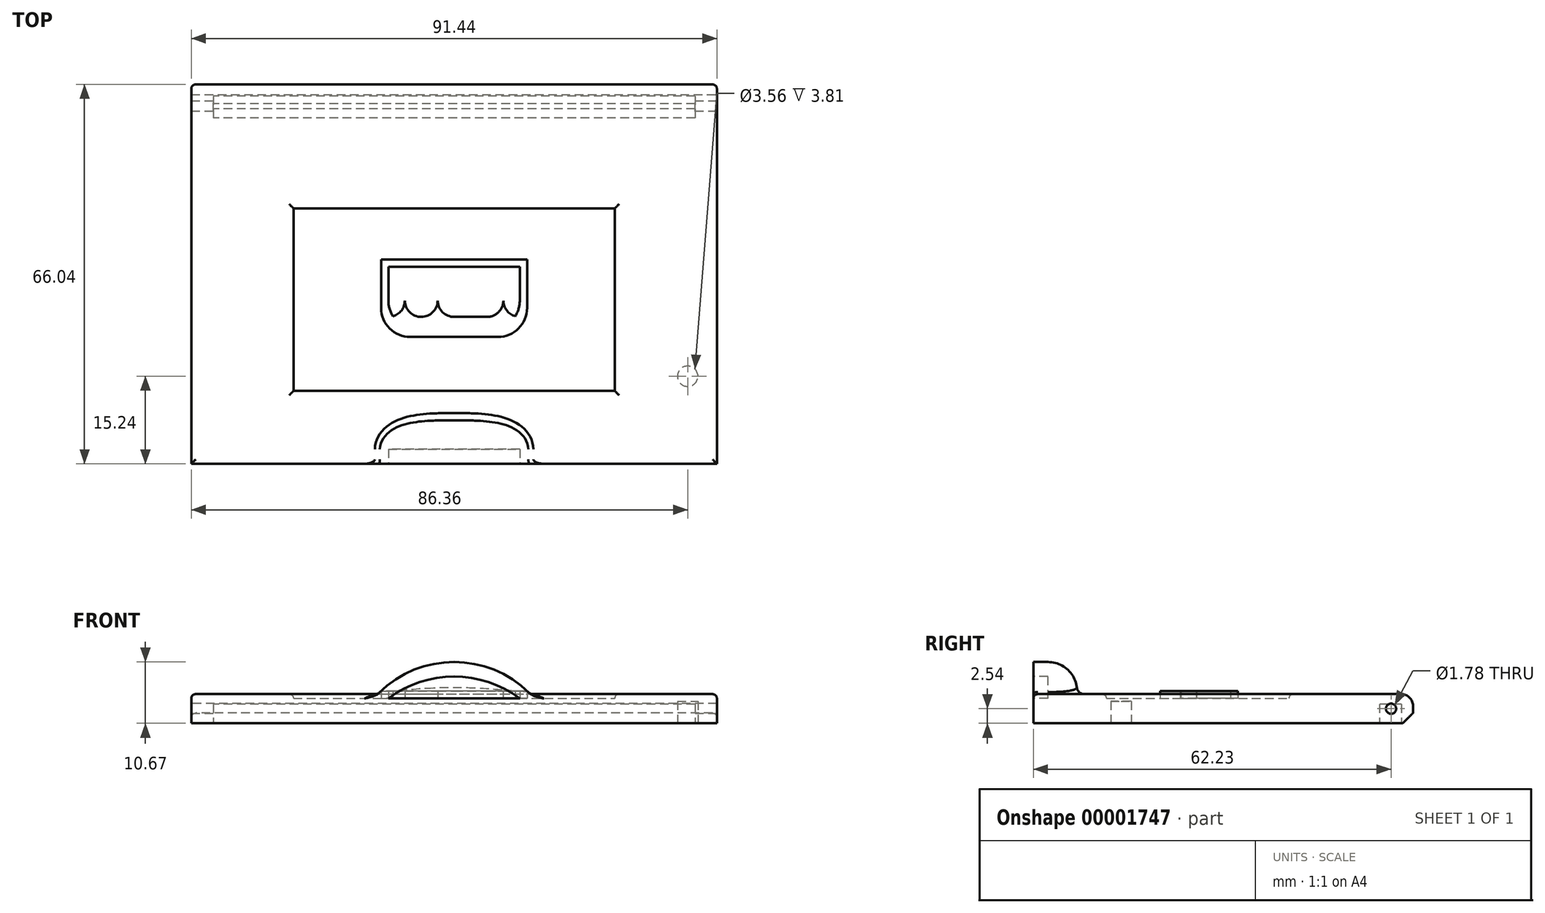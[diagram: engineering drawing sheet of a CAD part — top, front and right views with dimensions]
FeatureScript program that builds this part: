
annotation { "Feature Type Name" : "Feature", "Feature Type Description" : "" }
export const myFeature = defineFeature(function(context is Context, id is Id, definition is map)
    precondition{}
    {
        {
            var Q0;
            Q0=qCreatedBy(makeId("Top.planeOp"),FACE);
            var sketch = newSketch(context, id + "F0", { "sketchPlane" : qUnion([Q0])});
            skLineSegment(sketch, "E0.bottom", {"start": v(0, 0) * mm, "end": v(91.44, 0) * mm});
            skLineSegment(sketch, "E0.top", {"start": v(0, 66.04) * mm, "end": v(91.44, 66.04) * mm});
            skLineSegment(sketch, "E0.left", {"start": v(0, 0) * mm, "end": v(0, 66.04) * mm});
            skLineSegment(sketch, "E0.right", {"start": v(91.44, 0) * mm, "end": v(91.44, 66.04) * mm});
            skSolve(sketch);
        }
        {
            var Q0;
            Q0 = qSketchRegion(id + "F0", true);
            extrude(context, id + "F1", {"entities" : qUnion([Q0]), "depth" : 5.08 * mm});
        }
        {
            var Q0;
            Q0=makeQuery(id+"F1.opExtrude","SWEPT_FACE",FACE,{"disambiguationData":[OSD([sQuery(id+"F0.wireOp",EDGE,"E0.left")])]});
            var sketch = newSketch(context, id + "F2", { "sketchPlane" : qUnion([Q0])});
            skLineSegment(sketch, "E1", {"start": v(-66.04, 2.54) * mm, "end": v(-62.23, 2.54) * mm, "construction": true});
            skCircle(sketch, "E2", {"center": v(-62.23, 2.54) * mm, "radius": 0.89 * mm});
            skSolve(sketch);
        }
        {
            var Q0;
            Q0 = qSketchRegion(id + "F2", true);
            extrude(context, id + "F3", {"entities" : qUnion([Q0]), "operationType" : NewBodyOperationType.REMOVE, "oppositeDirection" : true, "depth" : 91.44 * mm});
        }
        {
            var Q0;
            Q0=makeQuery(id+"F1.opExtrude","CAP_FACE",FACE,{"disambiguationData":[OSD([sQuery(id+"F0.wireOp",EDGE,"E0.bottom"),sQuery(id+"F0.wireOp",EDGE,"E0.top"),sQuery(id+"F0.wireOp",EDGE,"E0.left"),sQuery(id+"F0.wireOp",EDGE,"E0.right")])],"isStart":true});
            var sketch = newSketch(context, id + "F4", { "sketchPlane" : qUnion([Q0])});
            skLineSegment(sketch, "E3", {"start": v(91.44, -66.04) * mm, "end": v(87.63, -66.04) * mm, "construction": true});
            skLineSegment(sketch, "E4", {"start": v(87.63, -66.04) * mm, "end": v(87.63, -64) * mm, "construction": true});
            skSolve(sketch);
        }
        {
            var Q0;
            Q0=makeQuery(id+"F4.imprint","IMPRINT",FACE,{"disambiguationData":[TD([[makeQuery(id+"F4.imprint","IMPRINT",EDGE,{"derivedFrom":makeQuery(id+"F1.opExtrude","CAP_EDGE",EDGE,{"disambiguationData":[OSD([sQuery(id+"F0.wireOp",EDGE,"E0.bottom")])],"isStart":true})}),-1.0]])]});
            var sketch = newSketch(context, id + "F5", { "sketchPlane" : qUnion([Q0])});
            skLineSegment(sketch, "E5.bottom", {"start": v(87.63, -64) * mm, "end": v(3.81, -64) * mm});
            skLineSegment(sketch, "E5.top", {"start": v(87.63, -60.2) * mm, "end": v(3.81, -60.2) * mm});
            skLineSegment(sketch, "E5.left", {"start": v(87.63, -64) * mm, "end": v(87.63, -60.2) * mm});
            skLineSegment(sketch, "E5.right", {"start": v(3.81, -64) * mm, "end": v(3.81, -60.2) * mm});
            skSolve(sketch);
        }
        {
            var Q0;
            Q0 = qSketchRegion(id + "F5", true);
            extrude(context, id + "F6", {"entities" : qUnion([Q0]), "operationType" : NewBodyOperationType.REMOVE, "oppositeDirection" : true, "depth" : 3.3 * mm});
        }
        {
            var Q0;
            Q0=makeQuery(id+"F1.opExtrude","CAP_EDGE",EDGE,{"disambiguationData":[OSD([sQuery(id+"F0.wireOp",EDGE,"E0.top")])],"isStart":true});
            chamfer(context, id + "F7", {"entities" : qUnion([Q0]), "width" : 1.78 * mm, "tangentPropagation" : true});
        }
        {
            var Q0;
            Q0=makeQuery(id+"F1.opExtrude","CAP_EDGE",EDGE,{"disambiguationData":[OSD([sQuery(id+"F0.wireOp",EDGE,"E0.top")])],"isStart":false});
            fillet(context, id + "F8", {"entities" : qUnion([Q0]), "radius" : 2.03 * mm, "tangentPropagation" : true, "allowEdgeOverflow" : false});
        }
        {
            var Q0;
            Q0=makeQuery(id+"F4.imprint","IMPRINT",FACE,{"disambiguationData":[TD([[makeQuery(id+"F4.imprint","IMPRINT",EDGE,{"derivedFrom":makeQuery(id+"F1.opExtrude","CAP_EDGE",EDGE,{"disambiguationData":[OSD([sQuery(id+"F0.wireOp",EDGE,"E0.bottom")])],"isStart":true})}),-1.0]])]});
            var sketch = newSketch(context, id + "F9", { "sketchPlane" : qUnion([Q0])});
            skLineSegment(sketch, "E6", {"start": v(91.44, 0) * mm, "end": v(91.44, -15.24) * mm, "construction": true});
            skLineSegment(sketch, "E7", {"start": v(91.44, -15.24) * mm, "end": v(86.36, -15.24) * mm, "construction": true});
            skSolve(sketch);
        }
        {
            var Q0;
            Q0=makeQuery(id+"F4.imprint","IMPRINT",FACE,{"disambiguationData":[TD([[makeQuery(id+"F4.imprint","IMPRINT",EDGE,{"derivedFrom":makeQuery(id+"F1.opExtrude","CAP_EDGE",EDGE,{"disambiguationData":[OSD([sQuery(id+"F0.wireOp",EDGE,"E0.bottom")])],"isStart":true})}),-1.0]])]});
            var sketch = newSketch(context, id + "F10", { "sketchPlane" : qUnion([Q0])});
            skCircle(sketch, "E8", {"center": v(86.36, -15.24) * mm, "radius": 1.78 * mm});
            skSolve(sketch);
        }
        {
            var Q0;
            Q0 = qSketchRegion(id + "F10", true);
            extrude(context, id + "F11", {"entities" : qUnion([Q0]), "operationType" : NewBodyOperationType.REMOVE, "oppositeDirection" : true, "depth" : 3.8 * mm});
        }
        {
            var Q0;
            Q0=makeQuery(id+"F1.opExtrude","CAP_FACE",FACE,{"disambiguationData":[OSD([sQuery(id+"F0.wireOp",EDGE,"E0.bottom"),sQuery(id+"F0.wireOp",EDGE,"E0.top"),sQuery(id+"F0.wireOp",EDGE,"E0.left"),sQuery(id+"F0.wireOp",EDGE,"E0.right")])],"isStart":false});
            var sketch = newSketch(context, id + "F12", { "sketchPlane" : qUnion([Q0])});
            skLineSegment(sketch, "E9", {"start": v(0, 0) * mm, "end": v(0, 12.7) * mm, "construction": true});
            skLineSegment(sketch, "E10", {"start": v(0, 12.7) * mm, "end": v(17.78, 12.7) * mm});
            skSolve(sketch);
        }
        {
            var Q0;
            {var subQ4=sQuery(id+"F0.wireOp",EDGE,"E0.bottom");var subQ7=makeQuery(id+"F1.opExtrude","CAP_EDGE",EDGE,{"disambiguationData":[OSD([subQ4])],"isStart":false});Q0=makeQuery(id+"F12.imprint","IMPRINT",FACE,{"disambiguationData":[TD([[makeQuery(id+"F12.imprint","IMPRINT",EDGE,{"derivedFrom":subQ7}),1.0]])]});}
            var sketch = newSketch(context, id + "F13", { "sketchPlane" : qUnion([Q0])});
            skLineSegment(sketch, "E11.bottom", {"start": v(17.78, 12.7) * mm, "end": v(73.66, 12.7) * mm});
            skLineSegment(sketch, "E11.top", {"start": v(17.78, 44.45) * mm, "end": v(73.66, 44.45) * mm});
            skLineSegment(sketch, "E11.left", {"start": v(17.78, 12.7) * mm, "end": v(17.78, 44.45) * mm});
            skLineSegment(sketch, "E11.right", {"start": v(73.66, 12.7) * mm, "end": v(73.66, 44.45) * mm});
            skSolve(sketch);
        }
        {
            var Q0;
            Q0 = qSketchRegion(id + "F13", true);
            extrude(context, id + "F14", {"entities" : qUnion([Q0]), "operationType" : NewBodyOperationType.REMOVE, "oppositeDirection" : true, "depth" : 0.76 * mm});
        }
        {
            var Q0;
            Q0=makeQuery(id+"F1.opExtrude","CAP_FACE",FACE,{"disambiguationData":[OSD([sQuery(id+"F0.wireOp",EDGE,"E0.bottom"),sQuery(id+"F0.wireOp",EDGE,"E0.top"),sQuery(id+"F0.wireOp",EDGE,"E0.left"),sQuery(id+"F0.wireOp",EDGE,"E0.right")])],"isStart":false});
            fillet(context, id + "F15", {"entities" : qUnion([Q0]), "radius" : 0.76 * mm, "tangentPropagation" : true, "allowEdgeOverflow" : false});
        }
        {
            var Q0;
            Q0=makeQuery(id+"F1.opExtrude","SWEPT_FACE",FACE,{"disambiguationData":[OSD([sQuery(id+"F0.wireOp",EDGE,"E0.bottom")])]});
            var sketch = newSketch(context, id + "F16", { "sketchPlane" : qUnion([Q0])});
            skLineSegment(sketch, "E12", {"start": v(45.72, 4.32) * mm, "end": v(31.75, 4.32) * mm, "construction": true});
            skLineSegment(sketch, "E13", {"start": v(45.72, 4.32) * mm, "end": v(59.7, 4.32) * mm, "construction": true});
            skLineSegment(sketch, "E14", {"start": v(45.72, 4.32) * mm, "end": v(45.72, 10.67) * mm, "construction": true});
            skArc(sketch, "E15", {"start": v(59.7, 4.32) * mm, "mid": v(45.72, 10.67) * mm, "end": v(31.75, 4.32) * mm});
            skLineSegment(sketch, "E16", {"start": v(31.75, 4.32) * mm, "end": v(59.7, 4.32) * mm});
            skSolve(sketch);
        }
        {
            var Q0;
            Q0=makeQuery(id+"F16.imprint","IMPRINT",FACE,{"disambiguationData":[TD([[makeQuery(id+"F16.imprint","IMPRINT",EDGE,{"derivedFrom":sQuery(id+"F16.wireOp",EDGE,"E15")}),1.0]])]});
            extrude(context, id + "F17", {"entities" : qUnion([Q0]), "operationType" : NewBodyOperationType.ADD, "oppositeDirection" : true, "depth" : 7.62 * mm});
        }
        {
            var Q0;
            Q0=makeQuery(id+"F17.opExtrude","CAP_EDGE",EDGE,{"disambiguationData":[OSD([sQuery(id+"F16.wireOp",EDGE,"E15")])],"isStart":false});
            fillet(context, id + "F18", {"entities" : qUnion([Q0]), "radius" : 5.08 * mm, "tangentPropagation" : true, "allowEdgeOverflow" : false});
        }
        {
            var Q0;
            Q0=makeQuery(id+"F17.boolean.opBoolean","MERGE",FACE,{"derivedFrom":[makeQuery(id+"F1.opExtrude","SWEPT_FACE",FACE,{"disambiguationData":[OSD([sQuery(id+"F0.wireOp",EDGE,"E0.bottom")])]}),makeQuery(id+"F17.opExtrude","CAP_FACE",FACE,{"disambiguationData":[OSD([sQuery(id+"F16.wireOp",EDGE,"E15"),sQuery(id+"F16.wireOp",EDGE,"E16")])],"isStart":true})]});
            var sketch = newSketch(context, id + "F19", { "sketchPlane" : qUnion([Q0])});
            skLineSegment(sketch, "E17", {"start": v(45.72, 10.67) * mm, "end": v(45.72, 8.13) * mm, "construction": true});
            skLineSegment(sketch, "E18", {"start": v(31.75, 4.32) * mm, "end": v(34.3, 4.32) * mm, "construction": true});
            skLineSegment(sketch, "E19", {"start": v(59.7, 4.32) * mm, "end": v(57.15, 4.32) * mm, "construction": true});
            skArc(sketch, "E20", {"start": v(57.15, 4.32) * mm, "mid": v(45.72, 8.13) * mm, "end": v(34.3, 4.32) * mm});
            skLineSegment(sketch, "E21", {"start": v(34.3, 4.32) * mm, "end": v(57.15, 4.32) * mm});
            skSolve(sketch);
        }
        {
            var Q0;
            Q0=makeQuery(id+"F19.imprint","IMPRINT",FACE,{"disambiguationData":[TD([[makeQuery(id+"F19.imprint","IMPRINT",EDGE,{"derivedFrom":sQuery(id+"F19.wireOp",EDGE,"E20")}),1.0]])]});
            extrude(context, id + "F20", {"entities" : qUnion([Q0]), "operationType" : NewBodyOperationType.REMOVE, "oppositeDirection" : true, "depth" : 2.54 * mm});
        }
        {
            var Q0;
            Q0=makeQuery(id+"F18.opFillet","BLEND_EDGE",EDGE,{"disambiguationData":[OD(0.0)],"blendedFrom":[makeQuery(id+"F17.opExtrude","CAP_EDGE",EDGE,{"disambiguationData":[OSD([sQuery(id+"F16.wireOp",EDGE,"E15")])],"isStart":false}),makeQuery(id+"F1.opExtrude","CAP_FACE",FACE,{"disambiguationData":[OSD([sQuery(id+"F0.wireOp",EDGE,"E0.bottom"),sQuery(id+"F0.wireOp",EDGE,"E0.top"),sQuery(id+"F0.wireOp",EDGE,"E0.left"),sQuery(id+"F0.wireOp",EDGE,"E0.right")])],"isStart":false})],"blendedInto":[makeQuery(id+"F1.opExtrude","CAP_FACE",FACE,{"disambiguationData":[OSD([sQuery(id+"F0.wireOp",EDGE,"E0.bottom"),sQuery(id+"F0.wireOp",EDGE,"E0.top"),sQuery(id+"F0.wireOp",EDGE,"E0.left"),sQuery(id+"F0.wireOp",EDGE,"E0.right")])],"isStart":false})]});
            fillet(context, id + "F21", {"entities" : qUnion([Q0]), "radius" : 1.27 * mm, "tangentPropagation" : true, "allowEdgeOverflow" : false});
        }
        {
            var Q0;
            Q0=makeQuery(id+"F14.boolean.opBoolean","COPY",FACE,{"derivedFrom":makeQuery(id+"F14.opExtrude","CAP_FACE",FACE,{"disambiguationData":[OSD([sQuery(id+"F13.wireOp",EDGE,"E11.bottom"),sQuery(id+"F13.wireOp",EDGE,"E11.top"),sQuery(id+"F13.wireOp",EDGE,"E11.left"),sQuery(id+"F13.wireOp",EDGE,"E11.right")])],"isStart":false})});
            var sketch = newSketch(context, id + "F22", { "sketchPlane" : qUnion([Q0])});
            skLineSegment(sketch, "E22", {"start": v(45.72, 12.7) * mm, "end": v(45.72, 25.4) * mm, "construction": true});
            skArc(sketch, "E23", {"start": v(39.95, 28.04) * mm, "mid": v(45.72, 19.05) * mm, "end": v(51.49, 28.04) * mm});
            skLineSegment(sketch, "E24", {"start": v(45.72, 25.4) * mm, "end": v(45.72, 40.64) * mm, "construction": true});
            skLineSegment(sketch, "E25", {"start": v(45.72, 40.64) * mm, "end": v(39.95, 28.04) * mm});
            skLineSegment(sketch, "E26", {"start": v(45.72, 40.64) * mm, "end": v(51.49, 28.04) * mm});
            skSolve(sketch);
        }
        {
            var Q0;
            Q0=makeQuery(id+"F14.boolean.opBoolean","COPY",FACE,{"derivedFrom":makeQuery(id+"F14.opExtrude","CAP_FACE",FACE,{"disambiguationData":[OSD([sQuery(id+"F13.wireOp",EDGE,"E11.bottom"),sQuery(id+"F13.wireOp",EDGE,"E11.top"),sQuery(id+"F13.wireOp",EDGE,"E11.left"),sQuery(id+"F13.wireOp",EDGE,"E11.right")])],"isStart":false})});
            var sketch = newSketch(context, id + "F23", { "sketchPlane" : qUnion([Q0])});
            skLineSegment(sketch, "E27", {"start": v(45.72, 44.45) * mm, "end": v(45.72, 35.55) * mm, "construction": true});
            skLineSegment(sketch, "E28", {"start": v(45.72, 35.55) * mm, "end": v(58.42, 35.55) * mm, "construction": true});
            skLineSegment(sketch, "E29.bottom", {"start": v(58.42, 35.55) * mm, "end": v(33.02, 35.55) * mm});
            skLineSegment(sketch, "E29.top", {"start": v(53.34, 22.07) * mm, "end": v(38.1, 22.07) * mm});
            skLineSegment(sketch, "E29.left", {"start": v(58.42, 35.55) * mm, "end": v(58.42, 27.15) * mm});
            skLineSegment(sketch, "E29.right", {"start": v(33.02, 35.55) * mm, "end": v(33.02, 27.15) * mm});
            skPoint(sketch, "E30.visualSharp", {"position": v(33.02, 22.07) * mm});
            skArc(sketch, "E30.filletArc", {"start": v(33.02, 27.15) * mm, "mid": v(34.5, 23.56) * mm, "end": v(38.1, 22.07) * mm});
            skPoint(sketch, "E31.visualSharp", {"position": v(58.42, 22.07) * mm});
            skArc(sketch, "E31.filletArc", {"start": v(53.34, 22.07) * mm, "mid": v(56.93, 23.56) * mm, "end": v(58.42, 27.15) * mm});
            skLineSegment(sketch, "E32.0", {"start": v(52.07, 23.34) * mm, "end": v(39.37, 23.34) * mm});
            skLineSegment(sketch, "E32.1", {"start": v(57.15, 34.28) * mm, "end": v(57.15, 28.42) * mm});
            skLineSegment(sketch, "E32.2", {"start": v(57.15, 34.28) * mm, "end": v(34.29, 34.28) * mm});
            skLineSegment(sketch, "E32.3", {"start": v(34.29, 34.28) * mm, "end": v(34.29, 28.42) * mm});
            skPoint(sketch, "E33.visualSharp", {"position": v(34.29, 23.34) * mm});
            skArc(sketch, "E33.filletArc", {"start": v(34.29, 28.42) * mm, "mid": v(35.78, 24.83) * mm, "end": v(39.37, 23.34) * mm});
            skPoint(sketch, "E34.visualSharp", {"position": v(57.15, 23.34) * mm});
            skArc(sketch, "E34.filletArc", {"start": v(52.07, 23.34) * mm, "mid": v(55.66, 24.83) * mm, "end": v(57.15, 28.42) * mm});
            skSolve(sketch);
        }
        {
            var Q0;
            Q0=makeQuery(id+"F23.imprint","IMPRINT",FACE,{"disambiguationData":[TD([[makeQuery(id+"F23.imprint","IMPRINT",EDGE,{"derivedFrom":sQuery(id+"F23.wireOp",EDGE,"E29.bottom")}),1.0]])]});
            extrude(context, id + "F24", {"entities" : qUnion([Q0]), "operationType" : NewBodyOperationType.ADD, "depth" : 1.27 * mm});
        }
        {
            var Q0;
            Q0=makeQuery(id+"F24.boolean.opBoolean","SPLIT",FACE,{"disambiguationData":[TD([makeQuery(id+"F24.opExtrude","SWEPT_FACE",FACE,{"disambiguationData":[OSD([sQuery(id+"F23.wireOp",EDGE,"E32.0")])]})])],"derivedFrom":makeQuery(id+"F14.boolean.opBoolean","COPY",FACE,{"derivedFrom":makeQuery(id+"F14.opExtrude","CAP_FACE",FACE,{"disambiguationData":[OSD([sQuery(id+"F13.wireOp",EDGE,"E11.bottom"),sQuery(id+"F13.wireOp",EDGE,"E11.top"),sQuery(id+"F13.wireOp",EDGE,"E11.left"),sQuery(id+"F13.wireOp",EDGE,"E11.right")])],"isStart":false})})});
            var sketch = newSketch(context, id + "F25", { "sketchPlane" : qUnion([Q0])});
            skLineSegment(sketch, "E35", {"start": v(34.29, 28.42) * mm, "end": v(40, 28.42) * mm, "construction": true});
            skLineSegment(sketch, "E36", {"start": v(40, 28.42) * mm, "end": v(45.72, 28.42) * mm, "construction": true});
            skLineSegment(sketch, "E37", {"start": v(45.72, 28.42) * mm, "end": v(51.43, 28.42) * mm, "construction": true});
            skLineSegment(sketch, "E38", {"start": v(51.43, 28.42) * mm, "end": v(57.15, 28.42) * mm, "construction": true});
            skLineSegment(sketch, "E39", {"start": v(57.15, 28.42) * mm, "end": v(57.15, 28.42) * mm});
            skArc(sketch, "E40", {"start": v(34.31, 25.57) * mm, "mid": v(36.32, 26.41) * mm, "end": v(37.15, 28.42) * mm});
            skArc(sketch, "E41", {"start": v(37.15, 28.42) * mm, "mid": v(40, 25.57) * mm, "end": v(42.86, 28.42) * mm});
            skArc(sketch, "E42", {"start": v(42.86, 28.42) * mm, "mid": v(45.72, 25.57) * mm, "end": v(48.58, 28.42) * mm});
            skArc(sketch, "E43", {"start": v(48.58, 28.42) * mm, "mid": v(51.43, 25.57) * mm, "end": v(54.3, 28.42) * mm});
            skArc(sketch, "E44", {"start": v(54.3, 28.42) * mm, "mid": v(55.14, 26.4) * mm, "end": v(57.17, 25.57) * mm});
            skLineSegment(sketch, "E45", {"start": v(31.43, 28.37) * mm, "end": v(60, 28.42) * mm});
            skLineSegment(sketch, "E46", {"start": v(34.31, 25.57) * mm, "end": v(57.17, 25.57) * mm});
            skSolve(sketch);
        }
        {
            var Q0;
            {var subQ3=makeQuery(id+"F24.opExtrude","CAP_EDGE",EDGE,{"disambiguationData":[OSD([sQuery(id+"F23.wireOp",EDGE,"E32.0")])],"isStart":true});Q0=makeQuery(id+"F25.imprint","IMPRINT",FACE,{"disambiguationData":[TD([[makeQuery(id+"F25.imprint","IMPRINT",EDGE,{"derivedFrom":subQ3}),-1.0]])]});}
            var Q1;
            {var subQ3=sQuery(id+"F25.wireOp",EDGE,"E40");var subQ7=sQuery(id+"F25.wireOp",EDGE,"E45");var subQ9=makeQuery(id+"F25.imprint","INTERSECT",VERTEX,{"derivedFrom":[subQ3,subQ7]});Q1=makeQuery(id+"F25.imprint","IMPRINT",FACE,{"disambiguationData":[TD([[makeQuery(id+"F25.imprint","IMPRINT",EDGE,{"disambiguationData":[TD([[subQ9,1.0]])],"derivedFrom":subQ3}),-1.0]])]});}
            var Q2;
            {var subQ0=sQuery(id+"F25.wireOp",EDGE,"E46");var subQ3=sQuery(id+"F25.wireOp",EDGE,"E41");var subQ4=makeQuery(id+"F25.imprint","INTERSECT",VERTEX,{"disambiguationData":[OD(1.0)],"derivedFrom":[subQ3,subQ0]});Q2=makeQuery(id+"F25.imprint","IMPRINT",FACE,{"disambiguationData":[TD([[makeQuery(id+"F25.imprint","IMPRINT",EDGE,{"disambiguationData":[TD([[subQ4,-1.0]])],"derivedFrom":subQ3}),-1.0]])]});}
            var Q3;
            {var subQ0=sQuery(id+"F25.wireOp",EDGE,"E46");var subQ3=sQuery(id+"F25.wireOp",EDGE,"E42");var subQ4=makeQuery(id+"F25.imprint","INTERSECT",VERTEX,{"disambiguationData":[OD(1.0)],"derivedFrom":[subQ3,subQ0]});Q3=makeQuery(id+"F25.imprint","IMPRINT",FACE,{"disambiguationData":[TD([[makeQuery(id+"F25.imprint","IMPRINT",EDGE,{"disambiguationData":[TD([[subQ4,-1.0]])],"derivedFrom":subQ3}),-1.0]])]});}
            var Q4;
            {var subQ1=sQuery(id+"F25.wireOp",EDGE,"E46");var subQ5=sQuery(id+"F25.wireOp",EDGE,"E43");var subQ6=makeQuery(id+"F25.imprint","INTERSECT",VERTEX,{"disambiguationData":[OD(1.0)],"derivedFrom":[subQ5,subQ1]});Q4=makeQuery(id+"F25.imprint","IMPRINT",FACE,{"disambiguationData":[TD([[makeQuery(id+"F25.imprint","IMPRINT",EDGE,{"disambiguationData":[TD([[subQ6,-1.0]])],"derivedFrom":subQ5}),-1.0]])]});}
            extrude(context, id + "F26", {"entities" : qUnion([Q0, Q1, Q2, Q3, Q4]), "operationType" : NewBodyOperationType.ADD, "depth" : 1.27 * mm});
        }
    });
